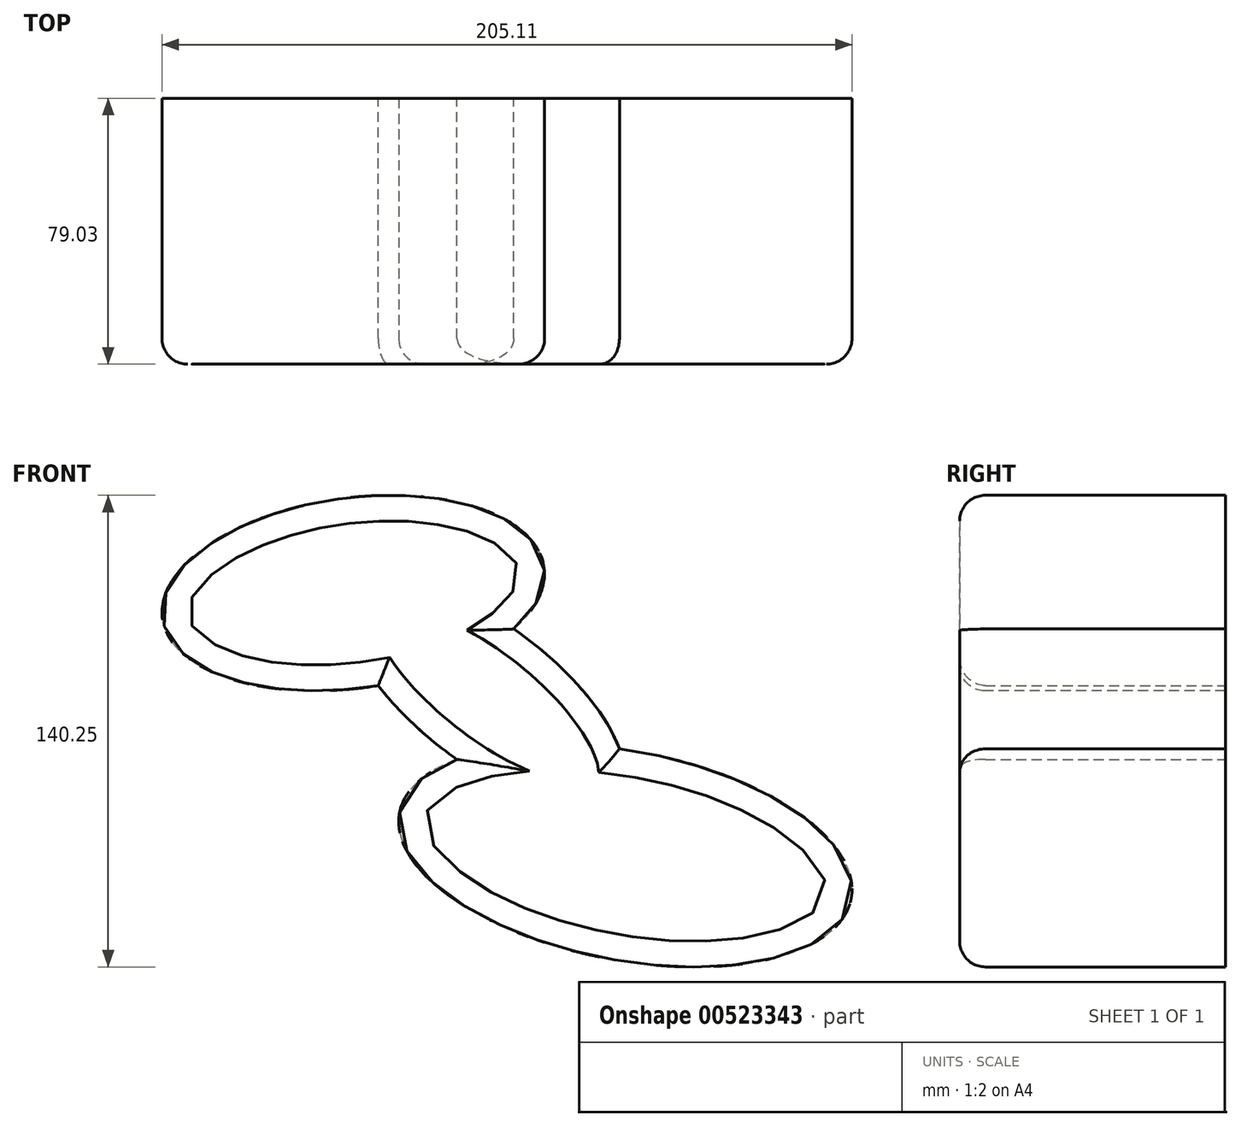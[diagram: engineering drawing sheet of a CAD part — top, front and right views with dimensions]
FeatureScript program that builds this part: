
annotation { "Feature Type Name" : "Feature", "Feature Type Description" : "" }
export const myFeature = defineFeature(function(context is Context, id is Id, definition is map)
    precondition{}
    {
        {
            var Q0;
            Q0=qCreatedBy(makeId("Front.planeOp"),FACE);
            var sketch = newSketch(context, id + "F0", { "sketchPlane" : qUnion([Q0])});
            skEllipse(sketch, "E0", {"center": v(-47, 37.62) * mm, "majorRadius": 57.24 * mm, "minorRadius": 28.31 * mm, "majorAxis": v(1, 0.13)});
            skEllipse(sketch, "E1", {"center": v(33.88, -40.47) * mm, "majorRadius": 68.33 * mm, "minorRadius": 31.06 * mm, "majorAxis": v(-0.98, 0.19)});
            skEllipse(sketch, "E2", {"center": v(-7.66, 7.5) * mm, "majorRadius": 49.55 * mm, "minorRadius": 20.65 * mm, "majorAxis": v(-0.8, 0.6)});
            skSolve(sketch);
        }
        {
            var Q0;
            Q0 = qSketchRegion(id + "F0", true);
            extrude(context, id + "F1", {"entities" : qUnion([Q0]), "depth" : 79.03 * mm, "offsetDistance" : 25.4 * mm});
        }
        {
            var Q0;
            Q0=makeQuery(id+"F1.opExtrude","CAP_EDGE",EDGE,{"disambiguationData":[OSD([sQuery(id+"F0.wireOp",EDGE,"E0")])],"isStart":false});
            var Q1;
            {var subQ0=sQuery(id+"F0.wireOp",EDGE,"E2");Q1=makeQuery(id+"F1.opExtrude","CAP_EDGE",EDGE,{"disambiguationData":[OSD([subQ0]),TDD([makeQuery(id+"F0.imprint","IMPRINT",EDGE,{"disambiguationData":[TD([[makeQuery(id+"F0.imprint","INTERSECT",VERTEX,{"disambiguationData":[OD(1.0)],"derivedFrom":[sQuery(id+"F0.wireOp",EDGE,"E0"),subQ0]}),1.0]])],"derivedFrom":subQ0})])],"isStart":false});}
            var Q2;
            {var subQ0=sQuery(id+"F0.wireOp",EDGE,"E2");Q2=makeQuery(id+"F1.opExtrude","CAP_EDGE",EDGE,{"disambiguationData":[OSD([subQ0]),TDD([makeQuery(id+"F0.imprint","IMPRINT",EDGE,{"disambiguationData":[TD([[makeQuery(id+"F0.imprint","INTERSECT",VERTEX,{"disambiguationData":[OD(0.0)],"derivedFrom":[sQuery(id+"F0.wireOp",EDGE,"E0"),subQ0]}),-1.0]])],"derivedFrom":subQ0})])],"isStart":false});}
            var Q3;
            Q3=makeQuery(id+"F1.opExtrude","CAP_EDGE",EDGE,{"disambiguationData":[OSD([sQuery(id+"F0.wireOp",EDGE,"E1")])],"isStart":false});
            fillet(context, id + "F2", {"entities" : qUnion([Q0, Q1, Q2, Q3]), "radius" : 7.62 * mm, "tangentPropagation" : true, "allowEdgeOverflow" : false});
        }
    });
